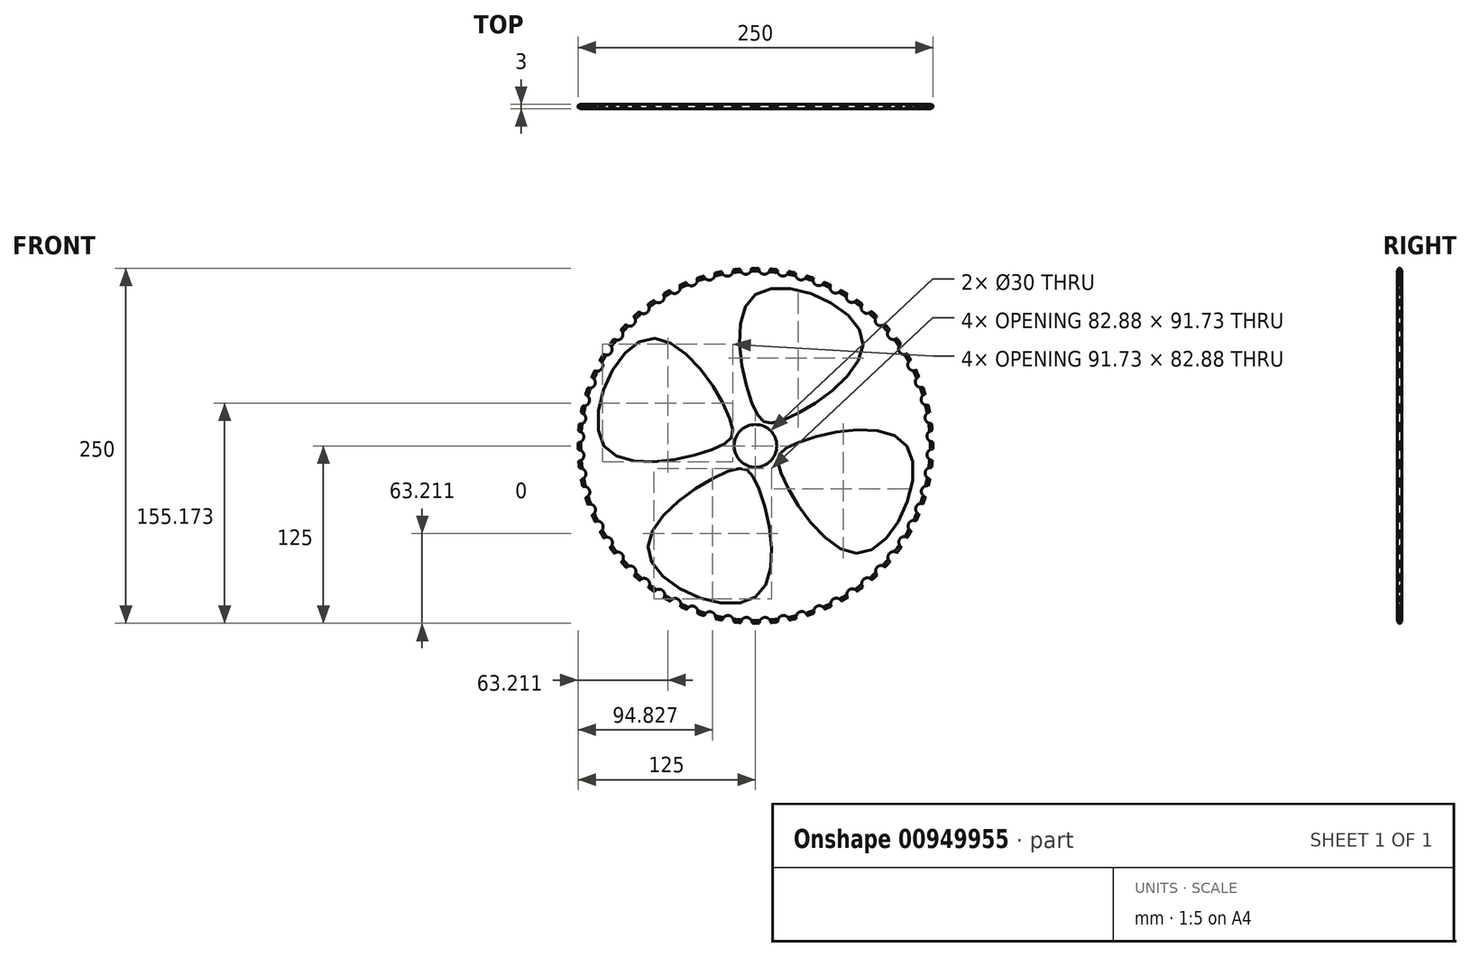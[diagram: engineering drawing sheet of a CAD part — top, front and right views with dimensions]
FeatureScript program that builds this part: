
annotation { "Feature Type Name" : "Feature", "Feature Type Description" : "" }
export const myFeature = defineFeature(function(context is Context, id is Id, definition is map)
    precondition{}
    {
        {
            var Q0;
            Q0=qCreatedBy(makeId("Front.planeOp"),FACE);
            var sketch = newSketch(context, id + "F0", { "sketchPlane" : qUnion([Q0])});
            skCircle(sketch, "E0", {"center": v(0, 0) * mm, "radius": 125 * mm});
            skSolve(sketch);
        }
        {
            var Q0;
            Q0=makeQuery(id+"F0.imprint","IMPRINT",FACE,{"disambiguationData":[TD([[makeQuery(id+"F0.imprint","IMPRINT",EDGE,{"derivedFrom":sQuery(id+"F0.wireOp",EDGE,"E0")}),1.0]])]});
            extrude(context, id + "F1", {"entities" : qUnion([Q0]), "depth" : 3 * mm, "offsetDistance" : 25 * mm});
        }
        {
            var Q0;
            {var subQ0=sQuery(id+"F0.wireOp",EDGE,"E0");Q0=makeQuery(id+"F6.boolean.opBoolean","SPLIT",EDGE,{"disambiguationData":[TD([makeQuery(id+"F1.opExtrude","SWEPT_FACE",FACE,{"disambiguationData":[OSD([subQ0])]}),makeQuery(id+"F1.opExtrude","CAP_FACE",FACE,{"disambiguationData":[OSD([subQ0])],"isStart":false}),makeQuery(id+"F6.opExtrude","SWEPT_FACE",FACE,{"disambiguationData":[OSD([sQuery(id+"F4.wireOp",EDGE,"E2.5.0")])]}),makeQuery(id+"F6.opExtrude","SWEPT_FACE",FACE,{"disambiguationData":[OSD([sQuery(id+"F4.wireOp",EDGE,"E2.6.0")])]})])],"derivedFrom":makeQuery(id+"F1.opExtrude","CAP_EDGE",EDGE,{"disambiguationData":[OSD([subQ0])],"isStart":false})});}
            chamfer(context, id + "F2", {"entities" : qUnion([Q0]), "chamferType" : ChamferType.TWO_OFFSETS, "width1" : 2 * mm, "oppositeDirection" : false, "width2" : 0.75 * mm, "tangentPropagation" : true});
        }
        {
            var Q0;
            {var subQ0=sQuery(id+"F0.wireOp",EDGE,"E0");Q0=makeQuery(id+"F6.boolean.opBoolean","SPLIT",EDGE,{"disambiguationData":[TD([makeQuery(id+"F1.opExtrude","SWEPT_FACE",FACE,{"disambiguationData":[OSD([subQ0])]}),makeQuery(id+"F1.opExtrude","CAP_FACE",FACE,{"disambiguationData":[OSD([subQ0])],"isStart":true}),makeQuery(id+"F6.opExtrude","SWEPT_FACE",FACE,{"disambiguationData":[OSD([sQuery(id+"F4.wireOp",EDGE,"E2.21.0")])]}),makeQuery(id+"F6.opExtrude","SWEPT_FACE",FACE,{"disambiguationData":[OSD([sQuery(id+"F4.wireOp",EDGE,"E2.22.0")])]})])],"derivedFrom":makeQuery(id+"F1.opExtrude","CAP_EDGE",EDGE,{"disambiguationData":[OSD([subQ0])],"isStart":true})});}
            chamfer(context, id + "F3", {"entities" : qUnion([Q0]), "chamferType" : ChamferType.TWO_OFFSETS, "width1" : 0.75 * mm, "oppositeDirection" : false, "width2" : 2 * mm, "tangentPropagation" : true});
        }
        {
            var Q0;
            Q0=makeQuery(id+"F1.opExtrude","CAP_FACE",FACE,{"disambiguationData":[OSD([sQuery(id+"F0.wireOp",EDGE,"E0")])],"isStart":false});
            var sketch = newSketch(context, id + "F4", { "sketchPlane" : qUnion([Q0])});
            skCircle(sketch, "E1", {"center": v(-111.48, 56.54) * mm, "radius": 4 * mm});
            skCircle(sketch, "E2.1.0", {"center": v(-116.78, 44.58) * mm, "radius": 4 * mm});
            skCircle(sketch, "E2.2.0", {"center": v(-120.8, 32.13) * mm, "radius": 4 * mm});
            skCircle(sketch, "E2.3.0", {"center": v(-123.5, 19.32) * mm, "radius": 4 * mm});
            skCircle(sketch, "E2.4.0", {"center": v(-124.84, 6.3) * mm, "radius": 4 * mm});
            skCircle(sketch, "E2.5.0", {"center": v(-124.82, -6.78) * mm, "radius": 4 * mm});
            skCircle(sketch, "E2.6.0", {"center": v(-123.42, -19.79) * mm, "radius": 4 * mm});
            skCircle(sketch, "E2.7.0", {"center": v(-120.68, -32.58) * mm, "radius": 4 * mm});
            skCircle(sketch, "E2.8.0", {"center": v(-116.61, -45.01) * mm, "radius": 4 * mm});
            skCircle(sketch, "E2.9.0", {"center": v(-111.27, -56.96) * mm, "radius": 4 * mm});
            skCircle(sketch, "E2.10.0", {"center": v(-104.7, -68.28) * mm, "radius": 4 * mm});
            skCircle(sketch, "E2.11.0", {"center": v(-97, -78.85) * mm, "radius": 4 * mm});
            skCircle(sketch, "E2.12.0", {"center": v(-88.22, -88.55) * mm, "radius": 4 * mm});
            skCircle(sketch, "E2.13.0", {"center": v(-78.48, -97.3) * mm, "radius": 4 * mm});
            skCircle(sketch, "E2.14.0", {"center": v(-67.88, -104.96) * mm, "radius": 4 * mm});
            skCircle(sketch, "E2.15.0", {"center": v(-56.54, -111.48) * mm, "radius": 4 * mm});
            skCircle(sketch, "E2.16.0", {"center": v(-44.58, -116.78) * mm, "radius": 4 * mm});
            skCircle(sketch, "E2.17.0", {"center": v(-32.13, -120.8) * mm, "radius": 4 * mm});
            skCircle(sketch, "E2.18.0", {"center": v(-19.32, -123.5) * mm, "radius": 4 * mm});
            skCircle(sketch, "E2.19.0", {"center": v(-6.3, -124.84) * mm, "radius": 4 * mm});
            skCircle(sketch, "E2.20.0", {"center": v(6.78, -124.82) * mm, "radius": 4 * mm});
            skCircle(sketch, "E2.21.0", {"center": v(19.79, -123.42) * mm, "radius": 4 * mm});
            skCircle(sketch, "E2.22.0", {"center": v(32.58, -120.68) * mm, "radius": 4 * mm});
            skCircle(sketch, "E2.23.0", {"center": v(45.01, -116.61) * mm, "radius": 4 * mm});
            skCircle(sketch, "E2.24.0", {"center": v(56.96, -111.27) * mm, "radius": 4 * mm});
            skCircle(sketch, "E2.25.0", {"center": v(68.28, -104.7) * mm, "radius": 4 * mm});
            skCircle(sketch, "E2.26.0", {"center": v(78.85, -97) * mm, "radius": 4 * mm});
            skCircle(sketch, "E2.27.0", {"center": v(88.55, -88.22) * mm, "radius": 4 * mm});
            skCircle(sketch, "E2.28.0", {"center": v(97.3, -78.48) * mm, "radius": 4 * mm});
            skCircle(sketch, "E2.29.0", {"center": v(104.96, -67.88) * mm, "radius": 4 * mm});
            skCircle(sketch, "E2.30.0", {"center": v(111.48, -56.54) * mm, "radius": 4 * mm});
            skCircle(sketch, "E2.31.0", {"center": v(116.78, -44.58) * mm, "radius": 4 * mm});
            skCircle(sketch, "E2.32.0", {"center": v(120.8, -32.13) * mm, "radius": 4 * mm});
            skCircle(sketch, "E2.33.0", {"center": v(123.5, -19.32) * mm, "radius": 4 * mm});
            skCircle(sketch, "E2.34.0", {"center": v(124.84, -6.3) * mm, "radius": 4 * mm});
            skCircle(sketch, "E2.35.0", {"center": v(124.82, 6.78) * mm, "radius": 4 * mm});
            skCircle(sketch, "E2.36.0", {"center": v(123.42, 19.79) * mm, "radius": 4 * mm});
            skCircle(sketch, "E2.37.0", {"center": v(120.68, 32.58) * mm, "radius": 4 * mm});
            skCircle(sketch, "E2.38.0", {"center": v(116.61, 45.01) * mm, "radius": 4 * mm});
            skCircle(sketch, "E2.39.0", {"center": v(111.27, 56.96) * mm, "radius": 4 * mm});
            skCircle(sketch, "E2.40.0", {"center": v(104.7, 68.28) * mm, "radius": 4 * mm});
            skCircle(sketch, "E2.41.0", {"center": v(97, 78.85) * mm, "radius": 4 * mm});
            skCircle(sketch, "E2.42.0", {"center": v(88.22, 88.55) * mm, "radius": 4 * mm});
            skCircle(sketch, "E2.43.0", {"center": v(78.48, 97.3) * mm, "radius": 4 * mm});
            skCircle(sketch, "E2.44.0", {"center": v(67.88, 104.96) * mm, "radius": 4 * mm});
            skCircle(sketch, "E2.45.0", {"center": v(56.54, 111.48) * mm, "radius": 4 * mm});
            skCircle(sketch, "E2.46.0", {"center": v(44.58, 116.78) * mm, "radius": 4 * mm});
            skCircle(sketch, "E2.47.0", {"center": v(32.13, 120.8) * mm, "radius": 4 * mm});
            skCircle(sketch, "E2.48.0", {"center": v(19.32, 123.5) * mm, "radius": 4 * mm});
            skCircle(sketch, "E2.49.0", {"center": v(6.3, 124.84) * mm, "radius": 4 * mm});
            skCircle(sketch, "E2.50.0", {"center": v(-6.78, 124.82) * mm, "radius": 4 * mm});
            skCircle(sketch, "E2.51.0", {"center": v(-19.79, 123.42) * mm, "radius": 4 * mm});
            skCircle(sketch, "E2.52.0", {"center": v(-32.58, 120.68) * mm, "radius": 4 * mm});
            skCircle(sketch, "E2.53.0", {"center": v(-45.01, 116.61) * mm, "radius": 4 * mm});
            skCircle(sketch, "E2.54.0", {"center": v(-56.96, 111.27) * mm, "radius": 4 * mm});
            skCircle(sketch, "E2.55.0", {"center": v(-68.28, 104.7) * mm, "radius": 4 * mm});
            skCircle(sketch, "E2.56.0", {"center": v(-78.85, 97) * mm, "radius": 4 * mm});
            skCircle(sketch, "E2.57.0", {"center": v(-88.55, 88.22) * mm, "radius": 4 * mm});
            skCircle(sketch, "E2.58.0", {"center": v(-97.3, 78.48) * mm, "radius": 4 * mm});
            skCircle(sketch, "E2.59.0", {"center": v(-104.96, 67.88) * mm, "radius": 4 * mm});
            skPoint(sketch, "E2.center", {"position": v(0, 0) * mm});
            skCircle(sketch, "E3", {"center": v(0, 0) * mm, "radius": 15 * mm});
            skCircle(sketch, "E4", {"center": v(0, 0) * mm, "radius": 24.55 * mm, "construction": true});
            skCircle(sketch, "E5", {"center": v(0, 0) * mm, "radius": 106.64 * mm, "construction": true});
            skLineSegment(sketch, "E6", {"start": v(0, 115.3) * mm, "end": v(0, -115.73) * mm, "construction": true});
            skLineSegment(sketch, "E7", {"start": v(-114.53, 0) * mm, "end": v(114.1, 0) * mm, "construction": true});
            skLineSegment(sketch, "E8.1.0", {"start": v(-80.99, -80.99) * mm, "end": v(80.68, 80.68) * mm, "construction": true});
            skLineSegment(sketch, "E8.2.0", {"start": v(0, -114.53) * mm, "end": v(0, 114.1) * mm, "construction": true});
            skLineSegment(sketch, "E8.3.0", {"start": v(80.99, -80.99) * mm, "end": v(-80.68, 80.68) * mm, "construction": true});
            skLineSegment(sketch, "E8.4.0", {"start": v(114.53, 0) * mm, "end": v(-114.1, 0) * mm, "construction": true});
            skLineSegment(sketch, "E8.5.0", {"start": v(80.99, 80.99) * mm, "end": v(-80.68, -80.68) * mm, "construction": true});
            skLineSegment(sketch, "E8.6.0", {"start": v(0, 114.53) * mm, "end": v(0, -114.1) * mm, "construction": true});
            skLineSegment(sketch, "E8.7.0", {"start": v(-80.99, 80.99) * mm, "end": v(80.68, -80.68) * mm, "construction": true});
            skFitSpline(sketch, "E9", {"points": [v(-106.64, 0) * mm, v(-75.4, 75.4) * mm, v(-17.36, 17.36) * mm, v(-24.55, 0) * mm, v(-106.64, 0) * mm]});
            skFitSpline(sketch, "E10", {"points": [v(0, 106.64) * mm, v(75.4, 75.4) * mm, v(17.36, 17.36) * mm, v(0, 24.55) * mm, v(0, 106.64) * mm]});
            skFitSpline(sketch, "E11", {"points": [v(106.64, 0) * mm, v(75.4, -75.4) * mm, v(17.36, -17.36) * mm, v(24.55, 0) * mm, v(106.64, 0) * mm]});
            skFitSpline(sketch, "E12", {"points": [v(0, -106.64) * mm, v(-75.4, -75.4) * mm, v(-17.36, -17.36) * mm, v(0, -24.55) * mm, v(0, -106.64) * mm]});
            skSolve(sketch);
        }
        {
            var Q0;
            {var subQ0=sQuery(id+"F4.wireOp",EDGE,"E1");var subQ1=makeQuery(id+"F1.opExtrude","CAP_EDGE",EDGE,{"disambiguationData":[OSD([sQuery(id+"F0.wireOp",EDGE,"E0")])],"isStart":false});var subQ2=makeQuery(id+"F4.imprint","INTERSECT",VERTEX,{"disambiguationData":[OD(0.0)],"derivedFrom":[subQ1,subQ0]});Q0=makeQuery(id+"F4.imprint","IMPRINT",FACE,{"disambiguationData":[TD([[makeQuery(id+"F4.imprint","IMPRINT",EDGE,{"disambiguationData":[TD([[subQ2,1.0]])],"derivedFrom":subQ0}),1.0]])]});}
            var Q1;
            {var subQ0=sQuery(id+"F4.wireOp",EDGE,"E1");var subQ1=makeQuery(id+"F1.opExtrude","CAP_EDGE",EDGE,{"disambiguationData":[OSD([sQuery(id+"F0.wireOp",EDGE,"E0")])],"isStart":false});var subQ2=makeQuery(id+"F4.imprint","INTERSECT",VERTEX,{"disambiguationData":[OD(0.0)],"derivedFrom":[subQ1,subQ0]});Q1=makeQuery(id+"F4.imprint","IMPRINT",FACE,{"disambiguationData":[TD([[makeQuery(id+"F4.imprint","IMPRINT",EDGE,{"disambiguationData":[TD([[subQ2,-1.0]])],"derivedFrom":subQ0}),1.0]])]});}
            extrude(context, id + "F5", {"entities" : qUnion([Q0, Q1]), "operationType" : NewBodyOperationType.REMOVE, "endBound" : BoundingType.THROUGH_ALL, "oppositeDirection" : true, "depth" : 25 * mm, "offsetDistance" : 25 * mm});
        }
        {
            var Q0;
            Q0 = qSketchRegion(id + "F4", true);
            extrude(context, id + "F6", {"entities" : qUnion([Q0]), "operationType" : NewBodyOperationType.REMOVE, "endBound" : BoundingType.THROUGH_ALL, "oppositeDirection" : true, "depth" : 25 * mm, "offsetDistance" : 25 * mm});
        }
    });
